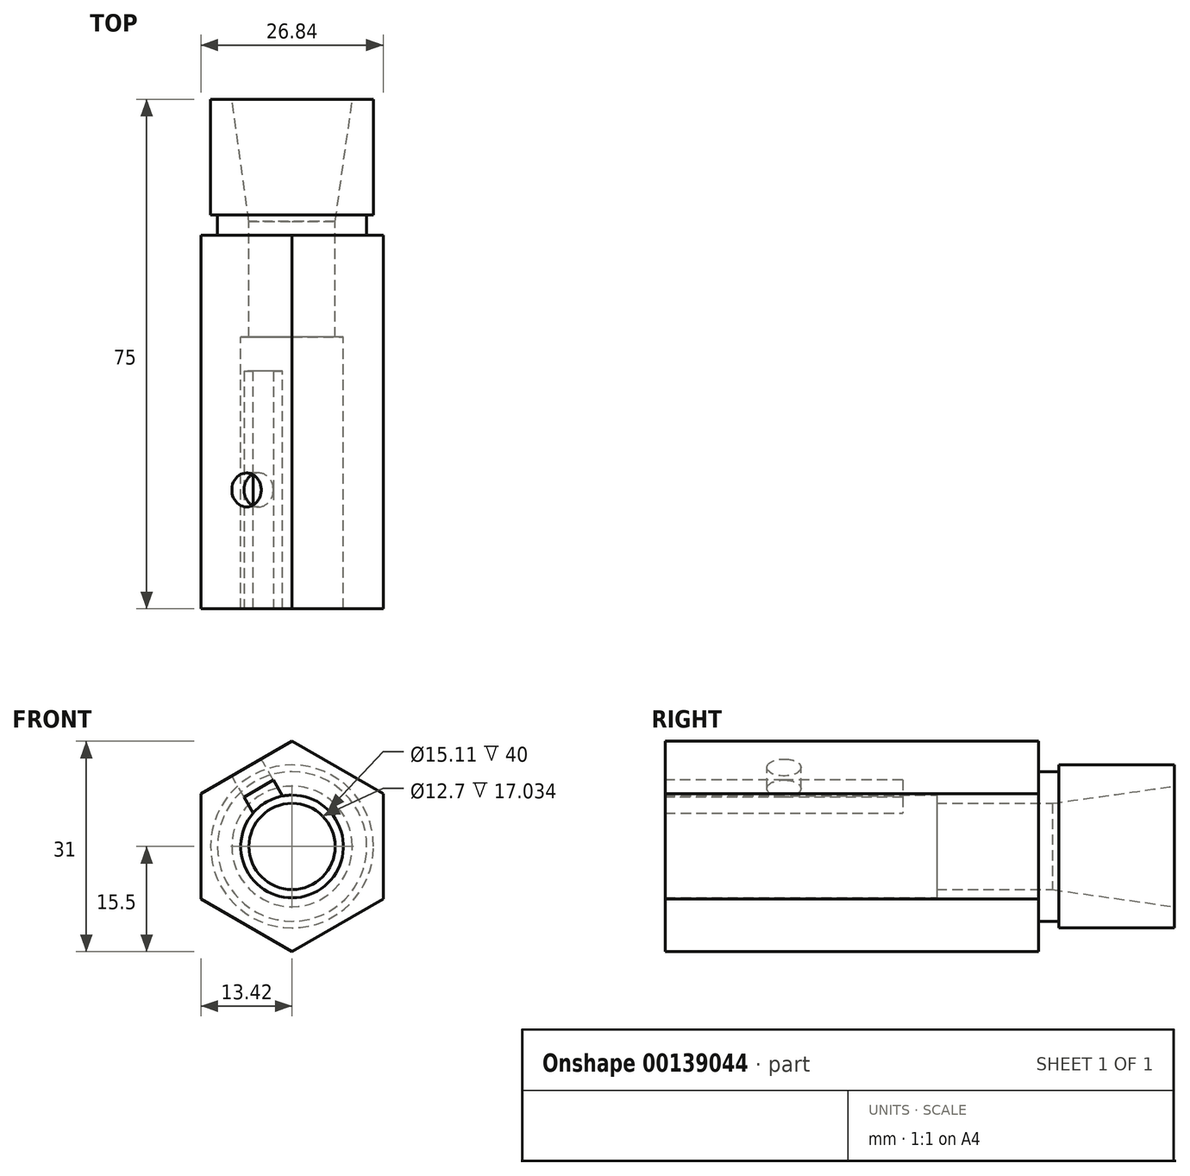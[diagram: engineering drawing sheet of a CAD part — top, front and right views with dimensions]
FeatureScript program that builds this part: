
annotation { "Feature Type Name" : "Feature", "Feature Type Description" : "" }
export const myFeature = defineFeature(function(context is Context, id is Id, definition is map)
    precondition{}
    {
        {
            var Q0;
            Q0=qCreatedBy(makeId("Front.planeOp"),FACE);
            var sketch = newSketch(context, id + "F0", { "sketchPlane" : qUnion([Q0])});
            skCircle(sketch, "E0", {"center": v(0, 0) * mm, "radius": 15.5 * mm});
            skSolve(sketch);
        }
        {
            var Q0;
            Q0 = qSketchRegion(id + "F0", true);
            extrude(context, id + "F1", {"entities" : qUnion([Q0]), "depth" : 75 * mm});
        }
        {
            var Q0;
            Q0=qCreatedBy(makeId("Right.planeOp"),FACE);
            var sketch = newSketch(context, id + "F2", { "sketchPlane" : qUnion([Q0])});
            skLineSegment(sketch, "E1", {"start": v(0, 0) * mm, "end": v(-80.95, 0) * mm, "construction": true});
            skLineSegment(sketch, "E2", {"start": v(0, 12) * mm, "end": v(-17, 12) * mm});
            skLineSegment(sketch, "E3", {"start": v(-17, 12) * mm, "end": v(-17, 11) * mm});
            skLineSegment(sketch, "E4", {"start": v(-17, 11) * mm, "end": v(-20, 11) * mm});
            skLineSegment(sketch, "E5", {"start": v(-20, 11) * mm, "end": v(-20, 15.5) * mm});
            skLineSegment(sketch, "E6", {"start": v(-20, 15.5) * mm, "end": v(0, 15.5) * mm});
            skLineSegment(sketch, "E7", {"start": v(0, 15.5) * mm, "end": v(0, 12) * mm});
            skLineSegment(sketch, "E8", {"start": v(-75, 15.5) * mm, "end": v(0, 15.5) * mm, "construction": true});
            skSolve(sketch);
        }
        {
            var Q0;
            Q0 = qSketchRegion(id + "F2", true);
            var Q1;
            Q1=sQuery(id+"F2.wireOp",EDGE,"E1");
            revolve(context, id + "F3", {"operationType" : NewBodyOperationType.REMOVE, "entities" : qUnion([Q0]), "axis" : qUnion([Q1]), "revolveType" : RevolveType.FULL, "oppositeDirection" : true});
        }
        {
            var Q0;
            Q0=makeQuery(id+"F3.boolean.opBoolean","COPY",FACE,{"derivedFrom":makeQuery(id+"F3.opRevolve","SWEPT_FACE",FACE,{"disambiguationData":[OSD([sQuery(id+"F2.wireOp",EDGE,"E5")])]})});
            var sketch = newSketch(context, id + "F4", { "sketchPlane" : qUnion([Q0])});
            skCircle(sketch, "E9.cCircle", {"center": v(0, 0) * mm, "radius": 15.5 * mm, "construction": true});
            skLineSegment(sketch, "E9.0", {"start": v(0, 15.5) * mm, "end": v(13.42, 7.75) * mm});
            skLineSegment(sketch, "E9.1", {"start": v(13.42, 7.75) * mm, "end": v(13.42, -7.75) * mm});
            skLineSegment(sketch, "E9.2", {"start": v(13.42, -7.75) * mm, "end": v(0, -15.5) * mm});
            skLineSegment(sketch, "E9.3", {"start": v(0, -15.5) * mm, "end": v(-13.42, -7.75) * mm});
            skLineSegment(sketch, "E9.4", {"start": v(-13.42, -7.75) * mm, "end": v(-13.42, 7.75) * mm});
            skLineSegment(sketch, "E9.5", {"start": v(-13.42, 7.75) * mm, "end": v(0, 15.5) * mm});
            skCircle(sketch, "E10", {"center": v(0, 0) * mm, "radius": 25.11 * mm});
            skSolve(sketch);
        }
        {
            var Q0;
            Q0 = qSketchRegion(id + "F4", true);
            extrude(context, id + "F5", {"entities" : qUnion([Q0]), "operationType" : NewBodyOperationType.REMOVE, "endBound" : BoundingType.THROUGH_ALL, "oppositeDirection" : true, "depth" : 25.4 * mm});
        }
        {
            var Q0;
            Q0=makeQuery(id+"F1.opExtrude","CAP_FACE",FACE,{"disambiguationData":[OSD([sQuery(id+"F0.wireOp",EDGE,"E0")])],"isStart":true});
            var sketch = newSketch(context, id + "F6", { "sketchPlane" : qUnion([Q0])});
            skCircle(sketch, "E11", {"center": v(0, 0) * mm, "radius": 7.56 * mm});
            skSolve(sketch);
        }
        {
            var Q0;
            Q0 = qSketchRegion(id + "F6", true);
            extrude(context, id + "F7", {"entities" : qUnion([Q0]), "operationType" : NewBodyOperationType.REMOVE, "endBound" : BoundingType.THROUGH_ALL, "oppositeDirection" : true, "depth" : 25.4 * mm});
        }
        {
            var Q0;
            Q0=makeQuery(id+"F1.opExtrude","CAP_FACE",FACE,{"disambiguationData":[OSD([sQuery(id+"F0.wireOp",EDGE,"E0")])],"isStart":false});
            var sketch = newSketch(context, id + "F8", { "sketchPlane" : qUnion([Q0])});
            skLineSegment(sketch, "E12", {"start": v(0, 0) * mm, "end": v(-6.71, 11.62) * mm, "construction": true});
            skLineSegment(sketch, "E13.bottom", {"start": v(-2.76, 9.79) * mm, "end": v(-7.1, 7.29) * mm});
            skLineSegment(sketch, "E13.top", {"start": v(-0.46, 5.8) * mm, "end": v(-4.8, 3.3) * mm});
            skLineSegment(sketch, "E13.left", {"start": v(-2.76, 9.79) * mm, "end": v(-0.46, 5.8) * mm});
            skLineSegment(sketch, "E13.right", {"start": v(-7.1, 7.29) * mm, "end": v(-4.8, 3.3) * mm});
            skPoint(sketch, "E13.middle", {"position": v(-3.78, 6.54) * mm});
            skSolve(sketch);
        }
        {
            var Q0;
            Q0 = qSketchRegion(id + "F8", true);
            extrude(context, id + "F9", {"entities" : qUnion([Q0]), "operationType" : NewBodyOperationType.REMOVE, "oppositeDirection" : true, "depth" : 35 * mm});
        }
        {
            var Q0;
            Q0=makeQuery(id+"F1.opExtrude","CAP_FACE",FACE,{"disambiguationData":[OSD([sQuery(id+"F0.wireOp",EDGE,"E0")])],"isStart":true});
            var sketch = newSketch(context, id + "F10", { "sketchPlane" : qUnion([Q0])});
            skCircle(sketch, "E14.0", {"center": v(0, 0) * mm, "radius": 7.56 * mm});
            skCircle(sketch, "E15", {"center": v(0, 0) * mm, "radius": 6.35 * mm});
            skSolve(sketch);
        }
        {
            var Q0;
            Q0 = qSketchRegion(id + "F10", true);
            extrude(context, id + "F11", {"entities" : qUnion([Q0]), "operationType" : NewBodyOperationType.ADD, "oppositeDirection" : true, "depth" : 35 * mm});
        }
        {
            var Q0;
            Q0=makeQuery(id+"F5.boolean.opBoolean","COPY",FACE,{"derivedFrom":makeQuery(id+"F5.opExtrude","SWEPT_FACE",FACE,{"disambiguationData":[OSD([sQuery(id+"F4.wireOp",EDGE,"E9.0")])]})});
            var sketch = newSketch(context, id + "F12", { "sketchPlane" : qUnion([Q0])});
            skPoint(sketch, "E16", {"position": v(0, -57.5) * mm});
            skLineSegment(sketch, "E17", {"start": v(0, -57.5) * mm, "end": v(11.87, -57.5) * mm, "construction": true});
            skSolve(sketch);
        }
        {
            var Q0;
            Q0=sQuery(id+"F12.wireOp",VERTEX,"E16");
            var Q1;
            Q1=makeQuery(id+"F1.opExtrude","SWEPT_BODY",BODY,{"disambiguationData":[OSD([sQuery(id+"F0.wireOp",EDGE,"E0")])]});
            hole(context, id + "F13", {"style" : HoleStyle.SIMPLE, "endStyle" : HoleEndStyle.BLIND, "holeDiameter" : 5 * mm, "holeDepth" : 15 * mm, "locations" : qUnion([Q0]), "scope" : qUnion([Q1])});
        }
        {
            var Q0;
            Q0=qCreatedBy(makeId("Right.planeOp"),FACE);
            var sketch = newSketch(context, id + "F14", { "sketchPlane" : qUnion([Q0])});
            skLineSegment(sketch, "E18", {"start": v(0, 0) * mm, "end": v(0, 8.88) * mm});
            skLineSegment(sketch, "E19", {"start": v(0, 8.88) * mm, "end": v(-20, 6.06) * mm});
            skLineSegment(sketch, "E20", {"start": v(-20, 6.06) * mm, "end": v(-20, 0) * mm});
            skLineSegment(sketch, "E21", {"start": v(-20, 0) * mm, "end": v(0, 0) * mm});
            skPoint(sketch, "E22", {"position": v(-12.86, 7.07) * mm});
            skSolve(sketch);
        }
        {
            var Q0;
            Q0 = qSketchRegion(id + "F14", true);
            var Q1;
            Q1=sQuery(id+"F14.wireOp",EDGE,"E21");
            revolve(context, id + "F15", {"operationType" : NewBodyOperationType.REMOVE, "entities" : qUnion([Q0]), "axis" : qUnion([Q1]), "revolveType" : RevolveType.FULL, "oppositeDirection" : true});
        }
    });
